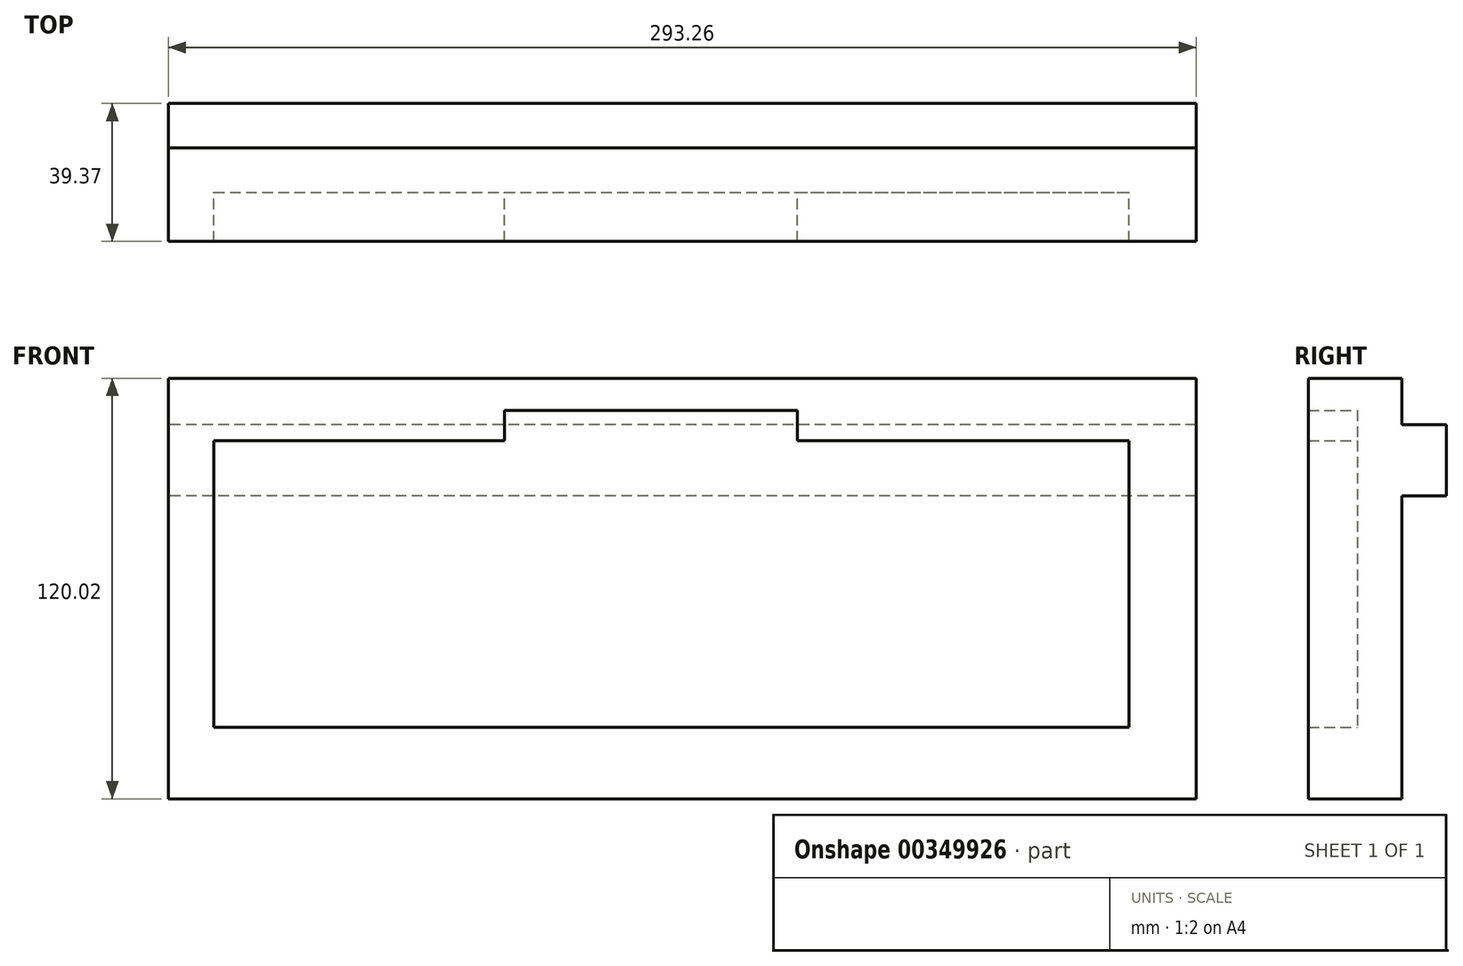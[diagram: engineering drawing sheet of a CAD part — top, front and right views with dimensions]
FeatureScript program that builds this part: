
annotation { "Feature Type Name" : "Feature", "Feature Type Description" : "" }
export const myFeature = defineFeature(function(context is Context, id is Id, definition is map)
    precondition{}
    {
        {
            var Q0;
            Q0=qCreatedBy(makeId("Front.planeOp"),FACE);
            var sketch = newSketch(context, id + "F0", { "sketchPlane" : qUnion([Q0])});
            skLineSegment(sketch, "E0.bottom", {"start": v(146.63, -60) * mm, "end": v(-146.63, -60) * mm});
            skLineSegment(sketch, "E0.top", {"start": v(146.63, 60) * mm, "end": v(-146.63, 60) * mm});
            skLineSegment(sketch, "E0.left", {"start": v(146.63, -60) * mm, "end": v(146.63, 60) * mm});
            skLineSegment(sketch, "E0.right", {"start": v(-146.63, -60) * mm, "end": v(-146.63, 60) * mm});
            skPoint(sketch, "E0.middle", {"position": v(0, 0) * mm});
            skSolve(sketch);
        }
        {
            var Q0;
            Q0 = qSketchRegion(id + "F0", true);
            extrude(context, id + "F1", {"entities" : qUnion([Q0]), "depth" : 12.7 * mm, "offsetDistance" : 25.4 * mm});
        }
        {
            var Q0;
            Q0=makeQuery(id+"F1.opExtrude","CAP_FACE",FACE,{"disambiguationData":[OSD([sQuery(id+"F0.wireOp",EDGE,"E0.bottom"),sQuery(id+"F0.wireOp",EDGE,"E0.top"),sQuery(id+"F0.wireOp",EDGE,"E0.left"),sQuery(id+"F0.wireOp",EDGE,"E0.right")])],"isStart":false});
            var sketch = newSketch(context, id + "F2", { "sketchPlane" : qUnion([Q0])});
            skLineSegment(sketch, "E1.bottom", {"start": v(-146.63, 60) * mm, "end": v(146.63, 60) * mm});
            skLineSegment(sketch, "E1.top", {"start": v(-146.63, 42.15) * mm, "end": v(146.63, 42.15) * mm});
            skLineSegment(sketch, "E1.left", {"start": v(-146.63, 60) * mm, "end": v(-146.63, 42.15) * mm});
            skLineSegment(sketch, "E1.right", {"start": v(146.63, 60) * mm, "end": v(146.63, 42.15) * mm});
            skLineSegment(sketch, "E2.bottom", {"start": v(-146.63, -60) * mm, "end": v(146.63, -60) * mm});
            skLineSegment(sketch, "E2.top", {"start": v(-146.63, -39.55) * mm, "end": v(146.63, -39.55) * mm});
            skLineSegment(sketch, "E2.left", {"start": v(-146.63, -60) * mm, "end": v(-146.63, -39.55) * mm});
            skLineSegment(sketch, "E2.right", {"start": v(146.63, -60) * mm, "end": v(146.63, -39.55) * mm});
            skLineSegment(sketch, "E3.bottom", {"start": v(-146.63, 42.15) * mm, "end": v(-133.62, 42.15) * mm});
            skLineSegment(sketch, "E3.top", {"start": v(-146.63, -39.55) * mm, "end": v(-133.62, -39.55) * mm});
            skLineSegment(sketch, "E3.left", {"start": v(-146.63, 42.15) * mm, "end": v(-146.63, -39.55) * mm});
            skLineSegment(sketch, "E3.right", {"start": v(-133.62, 42.15) * mm, "end": v(-133.62, -39.55) * mm});
            skLineSegment(sketch, "E4.bottom", {"start": v(146.63, 42.15) * mm, "end": v(127.44, 42.15) * mm});
            skLineSegment(sketch, "E4.top", {"start": v(146.63, -39.55) * mm, "end": v(127.44, -39.55) * mm});
            skLineSegment(sketch, "E4.left", {"start": v(146.63, 42.15) * mm, "end": v(146.63, -39.55) * mm});
            skLineSegment(sketch, "E4.right", {"start": v(127.44, 42.15) * mm, "end": v(127.44, -39.55) * mm});
            skSolve(sketch);
        }
        {
            var Q0;
            {var subQ3=sQuery(id+"F2.wireOp",EDGE,"E3.left");var subQ6=sQuery(id+"F2.wireOp",EDGE,"E4.left");Q0=qUnion([makeQuery(id+"F2.imprint","IMPRINT",FACE,{"disambiguationData":[TD([[makeQuery(id+"F2.imprint","IMPRINT",EDGE,{"derivedFrom":sQuery(id+"F2.wireOp",EDGE,"E1.bottom")}),1.0]])]}),makeQuery(id+"F2.imprint","IMPRINT",FACE,{"disambiguationData":[TD([[makeQuery(id+"F2.imprint","IMPRINT",EDGE,{"derivedFrom":subQ6}),1.0]])]}),makeQuery(id+"F2.imprint","IMPRINT",FACE,{"disambiguationData":[TD([[makeQuery(id+"F2.imprint","IMPRINT",EDGE,{"derivedFrom":subQ3}),-1.0]])]}),makeQuery(id+"F2.imprint","IMPRINT",FACE,{"disambiguationData":[TD([[makeQuery(id+"F2.imprint","IMPRINT",EDGE,{"derivedFrom":sQuery(id+"F2.wireOp",EDGE,"E2.bottom")}),-1.0]])]})]);}
            extrude(context, id + "F3", {"entities" : qUnion([Q0]), "operationType" : NewBodyOperationType.ADD, "depth" : 13.97 * mm, "offsetDistance" : 25.4 * mm});
        }
        {
            var Q0;
            Q0=makeQuery(id+"F1.opExtrude","CAP_FACE",FACE,{"disambiguationData":[OSD([sQuery(id+"F0.wireOp",EDGE,"E0.bottom"),sQuery(id+"F0.wireOp",EDGE,"E0.top"),sQuery(id+"F0.wireOp",EDGE,"E0.left"),sQuery(id+"F0.wireOp",EDGE,"E0.right")])],"isStart":true});
            var sketch = newSketch(context, id + "F4", { "sketchPlane" : qUnion([Q0])});
            skLineSegment(sketch, "E5.bottom", {"start": v(-146.63, 46.7) * mm, "end": v(146.63, 46.7) * mm});
            skLineSegment(sketch, "E5.top", {"start": v(-146.63, 26.46) * mm, "end": v(146.63, 26.46) * mm});
            skLineSegment(sketch, "E5.left", {"start": v(-146.63, 46.7) * mm, "end": v(-146.63, 26.46) * mm});
            skLineSegment(sketch, "E5.right", {"start": v(146.63, 46.7) * mm, "end": v(146.63, 26.46) * mm});
            skSolve(sketch);
        }
        {
            var Q0;
            Q0 = qSketchRegion(id + "F4", true);
            extrude(context, id + "F5", {"entities" : qUnion([Q0]), "operationType" : NewBodyOperationType.ADD, "depth" : 12.7 * mm, "offsetDistance" : 25.4 * mm});
        }
        {
            var Q0;
            Q0=makeQuery(id+"F3.opExtrude","SWEPT_FACE",FACE,{"disambiguationData":[OSD([sQuery(id+"F2.wireOp",EDGE,"E1.top")])]});
            var sketch = newSketch(context, id + "F6", { "sketchPlane" : qUnion([Q0])});
            skLineSegment(sketch, "E6.bottom", {"start": v(-50.68, 26.67) * mm, "end": v(32.8, 26.67) * mm});
            skLineSegment(sketch, "E6.top", {"start": v(-50.68, 12.7) * mm, "end": v(32.8, 12.7) * mm});
            skLineSegment(sketch, "E6.left", {"start": v(-50.68, 26.67) * mm, "end": v(-50.68, 12.7) * mm});
            skLineSegment(sketch, "E6.right", {"start": v(32.8, 26.67) * mm, "end": v(32.8, 12.7) * mm});
            skSolve(sketch);
        }
        {
            var Q0;
            Q0 = qSketchRegion(id + "F6", true);
            extrude(context, id + "F7", {"entities" : qUnion([Q0]), "operationType" : NewBodyOperationType.REMOVE, "oppositeDirection" : true, "depth" : 8.64 * mm, "offsetDistance" : 25.4 * mm});
        }
    });
